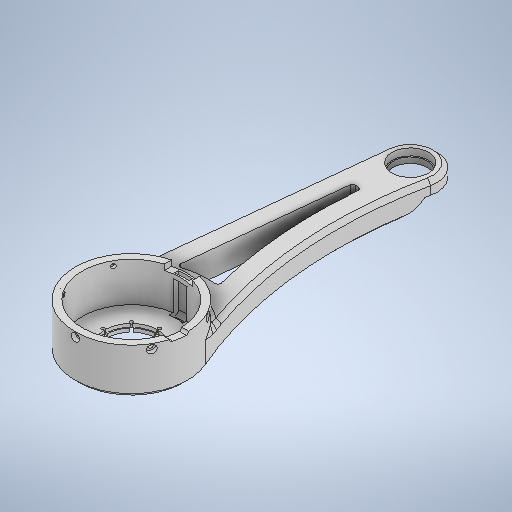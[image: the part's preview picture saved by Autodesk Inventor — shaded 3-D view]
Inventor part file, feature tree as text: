
AUTODESK INVENTOR PART (.ipt)
format: ipt  version: 2025.2 (Build 292293000, 293)  size: 1,806,848 bytes
history: native  units: mm
features: sketch x25, extrude x21, projected_geometry x21, fillet x6, plane x2, chamfer x2, pattern_circular x1, mirror x1, other x1
ambient origin geometry x8: Origin, YZ Plane, XZ Plane, XY Plane, X Axis, Y Axis, Z Axis, Center Point
bodies: Solid1 (feature_tree)
feature tree (80):
  extrude  "Extrusion1"  Depth=80.5mm
  extrude  "Extrusion2"  Depth=100.0mm
  extrude  "Extrusion3"  Depth=19.05mm
  extrude  "Extrusion4"  Depth=26.065mm
  extrude  "Extrusion5"  Depth=0.85mm
  extrude  "Extrusion6"  Depth=4.0mm
  extrude  "Extrusion7"  Depth=300.0mm
  extrude  "Extrusion8"  Depth=6.0mm TaperAngle=0.0deg
  extrude  "Extrusion9"  Depth=24.1mm TaperAngle=0.0deg
  extrude  "Extrusion12"  Depth=1.0mm
  extrude  "Extrusion13"  Depth=2.4mm TaperAngle=0.0deg
  extrude  "Extrusion14"  Depth=2.4mm
  extrude  "Extrusion15"  TaperAngle=0.0deg  [1 undecoded]
  extrude  "Extrusion16"  Depth=0.2mm
  plane  "Work Plane2"
  extrude  "Extrusion17"  Depth=0.2mm
  extrude  "Extrusion18"  Depth=2.5mm TaperAngle=0.0deg
  pattern_circular  "Circular Pattern1"  Count=8 Angle=360.0deg
  extrude  "Extrusion19"  Depth=0.8mm TaperAngle=0.0deg
  extrude  "Extrusion20"  Depth=0.8mm TaperAngle=0.0deg
  fillet  "Fillet2"  [1 undecoded]
  chamfer  "Chamfer1"  Distance=3.0mm
  fillet  "Fillet3"  Radius=3.0mm
  chamfer  "Chamfer2"  Distance=7.233mm
  extrude  "Extrusion21"  Depth=20.3mm
  extrude  "Extrusion22"  Depth=4.0mm TaperAngle=0.0deg
  fillet  "Fillet5"  Radius=12.0mm
  fillet  "Fillet6"  Radius=11.15mm
  extrude  "Extrusion23"  Depth=1.7mm TaperAngle=0.0deg
  fillet  "Fillet7"  Radius=3.0mm
  mirror  "Mirror1"
  fillet  "Fillet11"  Radius=3.0mm
  sketch  "Sketch1"  dims[d0=38.0mm d1=80.5mm]
  sketch  "Sketch2"  dims[d7=9.0mm d8=0.0mm d10=19.05mm]
  projected_geometry  "Projected Loop1"
  sketch  "Sketch3"  dims[d14=5.0mm d15=0.0mm d16=0.85mm]
  sketch  "Sketch4"  dims[d17=0.0mm d18=0.0mm d19=4.0mm]
  sketch  "Sketch5"  dims[d21=45.0deg d23=300.0mm]
  sketch  "Sketch Circular Pattern1"  dims[d2=200.0mm d3=100.0mm]
  projected_geometry  "Projected Loop2"
  sketch  "Sketch6"  dims[d24=40.0mm d26=360.0deg d28=6.0mm d29=0.0mm]
  sketch  "Sketch7"  dims[d33=34.0mm d34=1.0mm]
  sketch  "Sketch8"  dims[d40=40.5mm d41=2.4mm]
  sketch  "Sketch9"  dims[d42=80.0mm d44=360.0deg d46=0.0mm d47=0.0mm]
  sketch  "Sketch Circular Pattern2"  dims[d11=9.0mm d12=0.0mm d13=26.065mm]
  sketch  "Sketch12"  dims[d68=4.4mm d69=0.2mm]
  projected_geometry  "Projected Loop5"
  sketch  "Sketch Circular Pattern6"  dims[d30=70.5mm d31=24.1mm d32=0.0mm]
  sketch  "Sketch13"  dims[d70=2.2mm d71=0.2mm]
  projected_geometry  "Projected Loop6"
  sketch  "Sketch Circular Pattern7"  dims[d35=4.1mm d36=0.0mm d38=2.4mm d39=0.0mm]
  sketch  "Sketch14"  dims[d72=80.0mm d74=360.0deg d76=2.5mm d77=0.0mm]
  projected_geometry  "Projected Loop7"
  projected_geometry  "Projected Loop8"
  projected_geometry  "Projected Loop9"
  projected_geometry  "Projected Loop10"
  projected_geometry  "Projected Loop11"
  projected_geometry  "Projected Loop12"
  projected_geometry  "Projected Loop13"
  projected_geometry  "Projected Loop14"
  sketch  "Sketch15"  dims[d79=37.0mm]
  projected_geometry  "Projected Loop15"
  projected_geometry  "Projected Loop16"
  projected_geometry  "Projected Loop17"
  projected_geometry  "Projected Loop18"
  projected_geometry  "Projected Loop19"
  projected_geometry  "Projected Loop20"
  projected_geometry  "Projected Loop21"
  projected_geometry  "Projected Loop22"
  sketch  "Sketch16"  dims[d80=0.3mm]
  projected_geometry  "Projected Loop23"
  other  "Work Axis1"
  plane  "Work Plane1"
  sketch  "Sketch17"  dims[d81=0.2mm]
  sketch  "Sketch18"  dims[d82=0.2mm d83=80.0mm d85=360.0deg]
  sketch  "Sketch19"  dims[d87=0.0mm d88=0.0mm d89=0.8mm d90=0.0mm]
  sketch  "Sketch20"  dims[d91=0.1mm d92=0.0mm d93=0.8mm d94=0.0mm d95=-5.235988mm]
  sketch  "Sketch21"  dims[d96=3.35mm]
  sketch  "Sketch22"  dims[d97=5.7mm d98=3.0mm d99=0.0mm d100=3.0mm d101=7.233mm d102=0.0mm]
  sketch  "Sketch23"  dims[d103=50.0mm d104=240.0deg d106=20.3mm d107=4.0mm d108=0.0mm d109=12.0mm d110=11.15mm d111=1.7mm d112=0.0mm d114=3.0mm d115=2.0mm d116=45.0deg d117=3.0mm d118=3.0mm d119=2.0mm d120=45.0deg d121=1.2mm d122=1.2mm d123=5.0mm d124=5.0mm d125=27.1mm d126=0.0mm d127=24.0mm d128=0.0mm d130=2.9mm d131=2.9mm d132=15.0mm d134=15.0mm d135=15.0mm d136=0.0mm d137=0.0mm d138=2.0mm d139=1.7mm d146=3.0mm d141=0.0mm d142=0.0mm d143=0.0mm d144=0.0mm]
note: 2 required parameter values undecoded (feature->parameter linkage not recoverable at this tier; creation-order binding heuristic only, values carry confidence <= 0.55)
